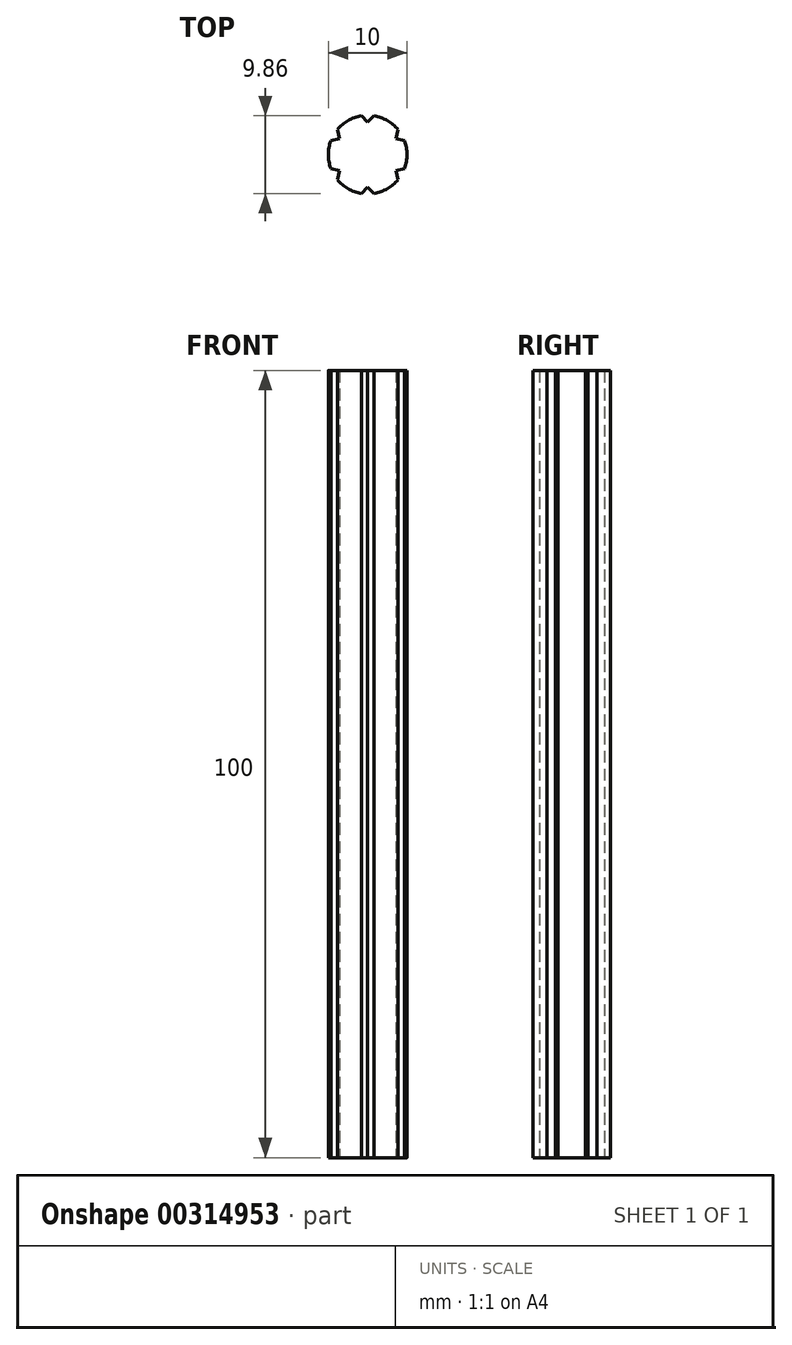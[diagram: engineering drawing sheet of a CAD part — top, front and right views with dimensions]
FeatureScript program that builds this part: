
annotation { "Feature Type Name" : "Feature", "Feature Type Description" : "" }
export const myFeature = defineFeature(function(context is Context, id is Id, definition is map)
    precondition{}
    {
        {
            assignVariable(context, id + "F0", {"name" : "height", "anyValue" : 100});
        }
        {
            assignVariable(context, id + "F1", {"name" : "notches", "anyValue" : 6});
        }
        {
            var Q0;
            Q0=qCreatedBy(makeId("Top.planeOp"),FACE);
            var sketch = newSketch(context, id + "F2", { "sketchPlane" : qUnion([Q0])});
            skCircle(sketch, "E0", {"center": v(0, 0) * mm, "radius": 5 * mm});
            skLineSegment(sketch, "E1", {"start": v(0, 0) * mm, "end": v(0, 5) * mm, "construction": true});
            skPoint(sketch, "E2.middle", {"position": v(0, 5) * mm});
            skSolve(sketch);
        }
        {
            var Q0;
            Q0=qCreatedBy(makeId("Top.planeOp"),FACE);
            var sketch = newSketch(context, id + "F3", { "sketchPlane" : qUnion([Q0])});
            skCircle(sketch, "E3", {"center": v(0, 0) * mm, "radius": 5 * mm});
            skLineSegment(sketch, "E4", {"start": v(0, 0) * mm, "end": v(0, 5) * mm, "construction": true});
            skLineSegment(sketch, "E5.bottom", {"start": v(0.88, 5) * mm, "end": v(0, 4.12) * mm});
            skLineSegment(sketch, "E5.top", {"start": v(0, 5.88) * mm, "end": v(-0.88, 5) * mm});
            skLineSegment(sketch, "E5.left", {"start": v(0.88, 5) * mm, "end": v(0, 5.88) * mm});
            skLineSegment(sketch, "E5.right", {"start": v(0, 4.12) * mm, "end": v(-0.88, 5) * mm});
            skPoint(sketch, "E5.middle", {"position": v(0, 5) * mm});
            skLineSegment(sketch, "E6", {"start": v(-0.88, 5) * mm, "end": v(0.88, 5) * mm});
            skSolve(sketch);
        }
        {
            var Q0;
            Q0=qSketchRegion(id+"F2",true);
            extrude(context, id + "F4", {"entities" : qUnion([Q0]), "depth" : (getVariable(context, 'height')) * mm});
        }
        {
            var Q0;
            {var subQ0=sQuery(id+"F3.wireOp",EDGE,"E5.bottom");var subQ1=sQuery(id+"F3.wireOp",EDGE,"E3");var subQ2=makeQuery(id+"F3.imprint","INTERSECT",VERTEX,{"derivedFrom":[subQ1,subQ0]});Q0=makeQuery(id+"F3.imprint","IMPRINT",FACE,{"disambiguationData":[TD([[makeQuery(id+"F3.imprint","IMPRINT",EDGE,{"disambiguationData":[TD([[subQ2,-1.0]])],"derivedFrom":subQ1}),1.0]])]});}
            extrude(context, id + "F5", {"entities" : qUnion([Q0]), "oppositeDirection" : true, "depth" : -(getVariable(context, 'height')) * mm});
        }
        {
            var Q0;
            Q0=makeQuery(id+"F5.opExtrude","SWEPT_BODY",BODY,{"disambiguationData":[OSD([sQuery(id+"F3.wireOp",EDGE,"E3"),sQuery(id+"F3.wireOp",EDGE,"E5.bottom"),sQuery(id+"F3.wireOp",EDGE,"E5.right")])]});
            var Q1;
            Q1=sQuery(id+"F2.wireOp",EDGE,"E0");
            circularPattern(context, id + "F6", {"operationType" : NewBodyOperationType.REMOVE, "entities" : qUnion([Q0]), "axis" : qUnion([Q1]), "angle" : 360 * degree, "instanceCount" : getVariable(context, 'notches'), "equalSpace" : true});
        }
    });
